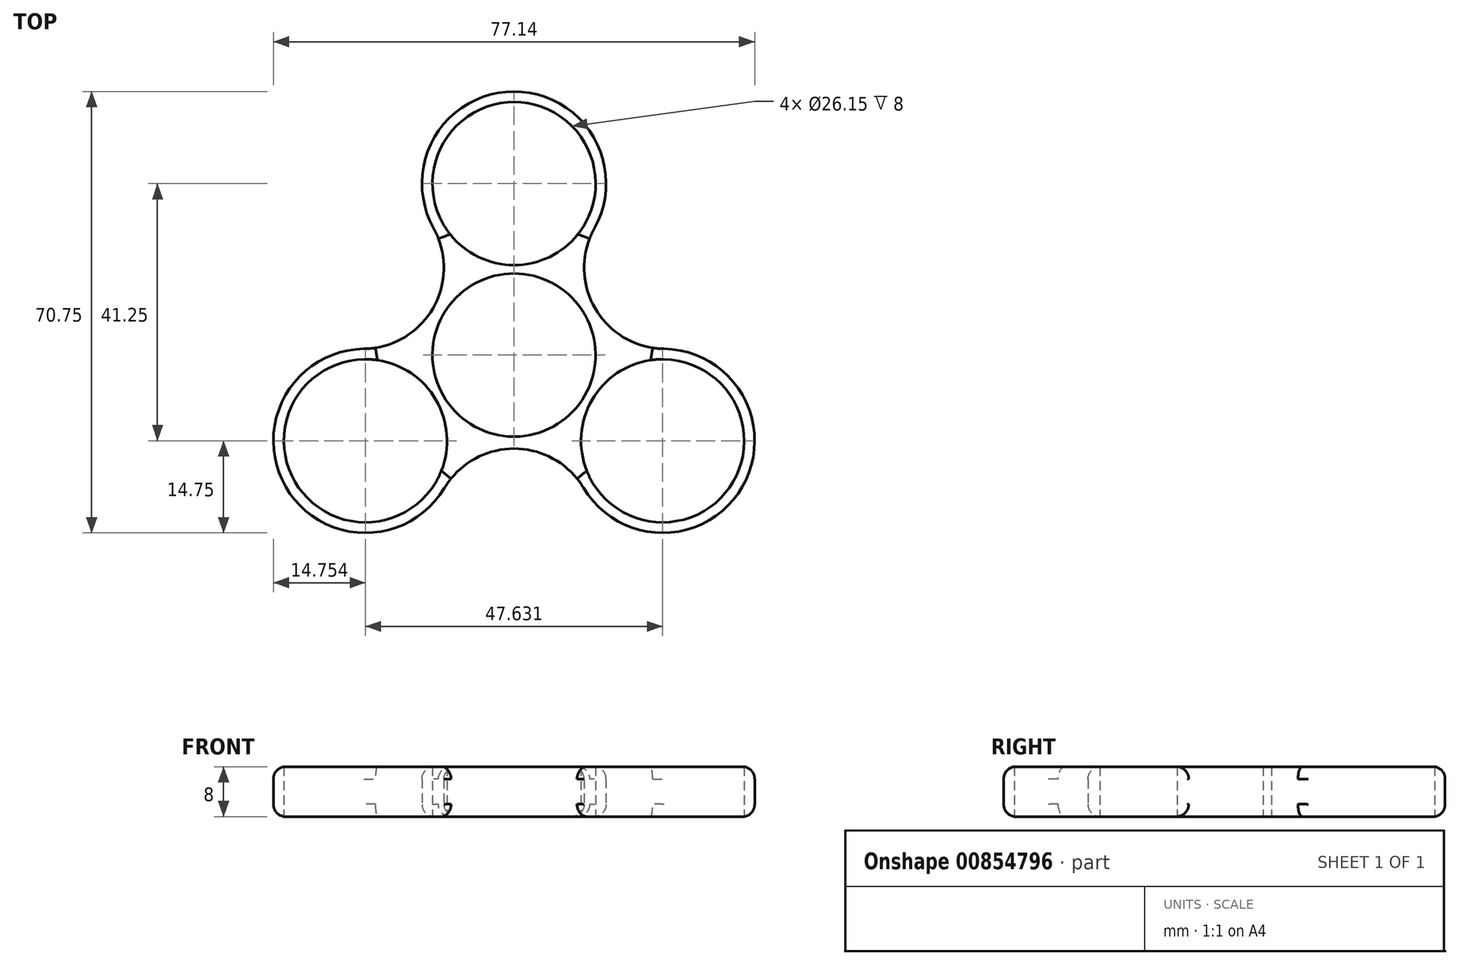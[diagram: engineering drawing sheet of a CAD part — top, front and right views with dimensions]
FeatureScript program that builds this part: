
annotation { "Feature Type Name" : "Feature", "Feature Type Description" : "" }
export const myFeature = defineFeature(function(context is Context, id is Id, definition is map)
    precondition{}
    {
        {
            var Q0;
            Q0=qCreatedBy(makeId("Top.planeOp"),FACE);
            var sketch = newSketch(context, id + "F0", { "sketchPlane" : qUnion([Q0])});
            skCircle(sketch, "E0", {"center": v(0, 27.5) * mm, "radius": 13.07 * mm});
            skCircle(sketch, "E1", {"center": v(-23.82, -13.75) * mm, "radius": 13.07 * mm});
            skCircle(sketch, "E2", {"center": v(0, 0) * mm, "radius": 27.5 * mm, "construction": true});
            skCircle(sketch, "E3", {"center": v(0, 0) * mm, "radius": 13.07 * mm});
            skLineSegment(sketch, "E4", {"start": v(0, 0) * mm, "end": v(-23.82, -13.75) * mm, "construction": true});
            skCircle(sketch, "E5.MirrorC", {"center": v(23.82, -13.75) * mm, "radius": 13.07 * mm});
            skPoint(sketch, "E6", {"position": v(-12.5, -7.21) * mm});
            skPoint(sketch, "E7", {"position": v(-11.32, -6.54) * mm});
            skSolve(sketch);
        }
        {
            var Q0;
            Q0=qCreatedBy(makeId("Top.planeOp"),FACE);
            var sketch = newSketch(context, id + "F1", { "sketchPlane" : qUnion([Q0])});
            skArc(sketch, "E8", {"start": v(12.9, 20.32) * mm, "mid": v(0, 42.25) * mm, "end": v(-12.9, 20.32) * mm});
            skArc(sketch, "E9", {"start": v(11.16, -21.33) * mm, "mid": v(36.6, -21.13) * mm, "end": v(24.05, 1) * mm});
            skArc(sketch, "E10", {"start": v(-24.05, 1) * mm, "mid": v(-36.6, -21.13) * mm, "end": v(-11.16, -21.33) * mm});
            skCircle(sketch, "E11", {"center": v(0, 27.5) * mm, "radius": 13.07 * mm});
            skCircle(sketch, "E12", {"center": v(23.82, -13.75) * mm, "radius": 13.07 * mm});
            skCircle(sketch, "E13", {"center": v(-23.82, -13.75) * mm, "radius": 13.07 * mm});
            skCircle(sketch, "E14", {"center": v(0, 0) * mm, "radius": 13.07 * mm});
            skArc(sketch, "E15", {"start": v(-24.05, 1) * mm, "mid": v(-13, 7.5) * mm, "end": v(-12.9, 20.32) * mm});
            skArc(sketch, "E16.1.0", {"start": v(11.16, -21.33) * mm, "mid": v(0, -15) * mm, "end": v(-11.16, -21.33) * mm});
            skArc(sketch, "E16.2.0", {"start": v(12.9, 20.32) * mm, "mid": v(13, 7.5) * mm, "end": v(24.05, 1) * mm});
            skPoint(sketch, "E17.orphan", {"position": v(-12.9, 20.32) * mm});
            skLineSegment(sketch, "E18", {"start": v(0, 27.5) * mm, "end": v(12.9, 20.32) * mm, "construction": true});
            skPoint(sketch, "E19", {"position": v(11.42, 21.14) * mm});
            skPoint(sketch, "E20", {"position": v(0, 13.07) * mm});
            skPoint(sketch, "E21", {"position": v(0, 14.43) * mm});
            skSolve(sketch);
        }
        {
            var Q0;
            Q0 = qSketchRegion(id + "F1", true);
            extrude(context, id + "F2", {"entities" : qUnion([Q0]), "depth" : 8 * mm, "offsetDistance" : 25 * mm});
        }
        {
            var Q0;
            Q0=makeQuery(id+"F2.opExtrude","CAP_EDGE",EDGE,{"disambiguationData":[OSD([sQuery(id+"F1.wireOp",EDGE,"E16.2.0")])],"isStart":false});
            fillet(context, id + "F3", {"entities" : qUnion([Q0]), "radius" : 2 * mm, "tangentPropagation" : true, "allowEdgeOverflow" : false});
        }
        {
            var Q0;
            Q0=makeQuery(id+"F2.opExtrude","CAP_EDGE",EDGE,{"disambiguationData":[OSD([sQuery(id+"F1.wireOp",EDGE,"E8")])],"isStart":true});
            fillet(context, id + "F4", {"entities" : qUnion([Q0]), "radius" : 2 * mm, "tangentPropagation" : true, "allowEdgeOverflow" : false});
        }
    });
